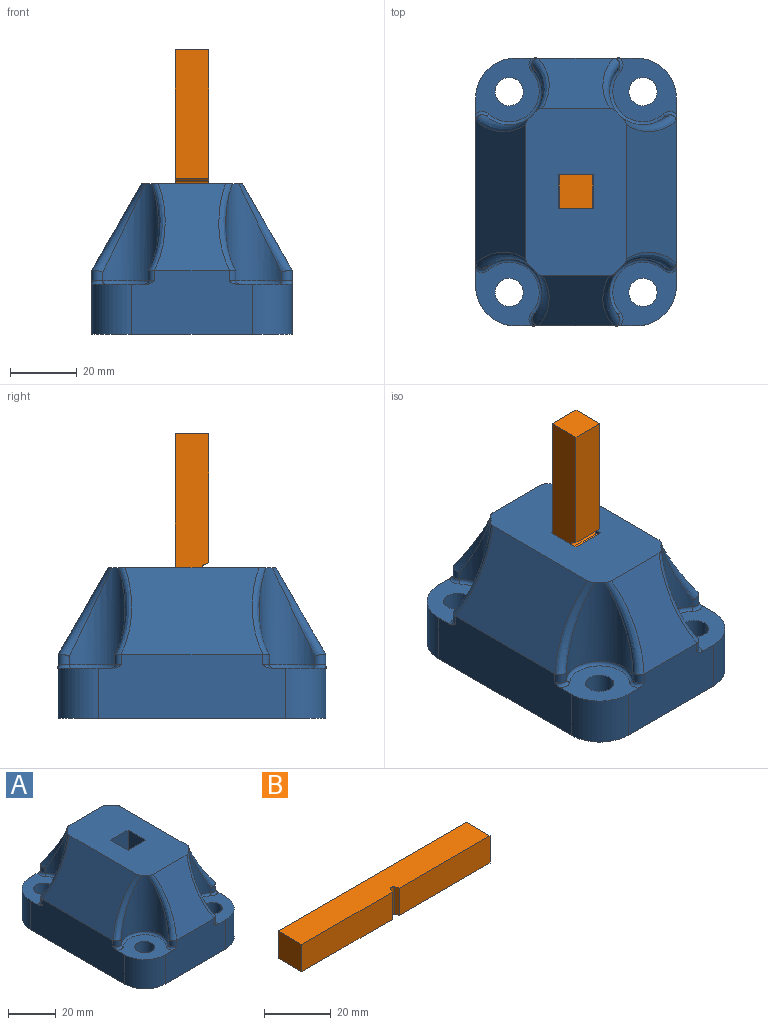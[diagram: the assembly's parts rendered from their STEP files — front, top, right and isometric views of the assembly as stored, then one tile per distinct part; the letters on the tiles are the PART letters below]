
ASSEMBLY  parts=2 mates=1
PART A: 59 faces, bbox 64.3x84.3x46.3 mm
  f0: plane 25.99x22.59mm, normal (0,0.87,0.5), area 532mm2, adj f8,f13,f31,f32,f35,f36
  f1: plane 42.59x25.99mm, normal (-0.87,0,0.5), area 1132mm2, adj f8,f11,f33,f34,f45,f46
  f2: cylinder r=12mm len=15mm, axis (0,0,-1), area 282.7mm2, adj f9,f11,f13,f29
  f3: plane 42.59x25.99mm, normal (0.87,0,0.5), area 1132mm2, adj f8,f10,f37,f38,f41,f42
  f4: cylinder r=12mm len=15mm, axis (0,0,1), area 282.7mm2, adj f9,f10,f13,f26
  f5: plane 25.99x22.59mm, normal (0,-0.87,0.5), area 532mm2, adj f8,f12,f39,f40,f43,f44
  f6: cylinder r=12mm len=15mm, axis (0,0,-1), area 282.7mm2, adj f9,f10,f12,f23
  f7: cylinder r=12mm len=15mm, axis (0,0,1), area 282.7mm2, adj f9,f11,f12,f20
  f8: plane 50.19x30.19mm, normal (0,0,1), area 1362.3mm2, adj f0,f1,f3,f5,f14,f15,f16,f17
  f9: plane 80x60mm, normal (0,0,-1), area 4454.7mm2, adj f2,f4,f6,f7,f10,f11,f12,f13
  f10: plane 56.31x19.33mm, normal (1,0,0), area 1010.9mm2, adj f3,f4,f6,f9,f23,f26,f37,f41
  f11: plane 56.31x19.33mm, normal (-1,0,0), area 1010.9mm2, adj f1,f2,f7,f9,f20,f29,f33,f45
  f12: plane 36.31x19.33mm, normal (0,-1,0), area 630.5mm2, adj f5,f6,f7,f9,f20,f23,f39,f43
  f13: plane 36.31x19.33mm, normal (0,1,0), area 630.5mm2, adj f0,f2,f4,f9,f26,f29,f31,f35
  f14: plane 40x10.2mm, normal (0,1,0), area 408mm2, adj f8,f15,f17,f18
  f15: plane 40x10.2mm, normal (-1,0,0), area 408mm2, adj f8,f14,f16,f18
  f16: plane 40x10.2mm, normal (0,-1,0), area 408mm2, adj f8,f15,f17,f18
  f17: plane 40x10.2mm, normal (1,0,0), area 408mm2, adj f8,f14,f16,f18
  f18: plane 10.2x10.2mm, normal (0,0,1), area 104mm2, adj f14,f15,f16,f17
  f19: cylinder r=4.2mm len=15mm, axis (0,0,1), area 395.8mm2, adj f9,f20
  f20: plane 19x19mm, normal (0,0,1), area 226.1mm2, adj f7,f11,f12,f19,f47,f48,f49
  f21: cylinder r=10mm len=29mm, axis (0,0,1), area 511.6mm2, adj f8,f43,f44,f45,f46,f48
  f22: cylinder r=4.2mm len=15mm, axis (0,0,1), area 395.8mm2, adj f9,f23
  f23: plane 19x19mm, normal (0,0,1), area 226.1mm2, adj f6,f10,f12,f22,f50,f51,f52
  f24: cylinder r=10mm len=29mm, axis (0,0,1), area 511.6mm2, adj f8,f39,f40,f41,f42,f51
  f25: cylinder r=4.2mm len=15mm, axis (0,0,1), area 395.8mm2, adj f9,f26
  f26: plane 19x19mm, normal (0,0,1), area 226.1mm2, adj f4,f10,f13,f25,f53,f54,f55
  f27: cylinder r=10mm len=29mm, axis (0,0,1), area 511.6mm2, adj f8,f35,f36,f37,f38,f54
  f28: cylinder r=4.2mm len=15mm, axis (0,0,1), area 395.8mm2, adj f9,f29
  f29: plane 19x19mm, normal (0,0,1), area 226.1mm2, adj f2,f11,f13,f28,f56,f57,f58
  f30: cylinder r=10mm len=29mm, axis (0,0,1), area 511.6mm2, adj f8,f31,f32,f33,f34,f57
  f31: cylinder r=2mm len=3.33mm, axis (0,0,1), area 13.7mm2, adj f0,f13,f30,f32,f56
  f32: bspline ~28.08x16.15mm, area 97.8mm2, adj f0,f8,f30,f31
  f33: cylinder r=2mm len=3.33mm, axis (0,0,1), area 13.7mm2, adj f1,f11,f30,f34,f58
  f34: bspline ~28.08x16.15mm, area 97.8mm2, adj f1,f8,f30,f33
  f35: cylinder r=2mm len=3.33mm, axis (0,0,1), area 13.7mm2, adj f0,f13,f27,f36,f55
  f36: bspline ~28.08x16.15mm, area 97.8mm2, adj f0,f8,f27,f35
  f37: cylinder r=2mm len=3.33mm, axis (0,0,1), area 13.7mm2, adj f3,f10,f27,f38,f53
  f38: bspline ~28.08x16.15mm, area 97.8mm2, adj f3,f8,f27,f37
  f39: cylinder r=2mm len=3.33mm, axis (0,0,1), area 13.7mm2, adj f5,f12,f24,f40,f50
  f40: bspline ~28.08x16.15mm, area 97.8mm2, adj f5,f8,f24,f39
  f41: cylinder r=2mm len=3.33mm, axis (0,0,1), area 13.7mm2, adj f3,f10,f24,f42,f52
  f42: bspline ~28.08x16.15mm, area 97.8mm2, adj f3,f8,f24,f41
  f43: cylinder r=2mm len=3.33mm, axis (0,0,1), area 13.7mm2, adj f5,f12,f21,f44,f49
  f44: bspline ~28.08x16.15mm, area 97.8mm2, adj f5,f8,f21,f43
  f45: cylinder r=2mm len=3.33mm, axis (0,0,1), area 13.7mm2, adj f1,f11,f21,f46,f47
  f46: bspline ~28.08x16.15mm, area 97.8mm2, adj f1,f8,f21,f45
  f47: torus R=3mm, axis (0,0,1), area 6.9mm2, adj f11,f20,f45,f48
  f48: torus R=9mm, axis (0,0,1), area 45.9mm2, adj f20,f21,f47,f49
  f49: torus R=3mm, axis (0,0,1), area 6.9mm2, adj f12,f20,f43,f48
  f50: torus R=3mm, axis (0,0,1), area 6.9mm2, adj f12,f23,f39,f51
  f51: torus R=9mm, axis (0,0,1), area 45.9mm2, adj f23,f24,f50,f52
  f52: torus R=3mm, axis (0,0,1), area 6.9mm2, adj f10,f23,f41,f51
  f53: torus R=3mm, axis (0,0,1), area 6.9mm2, adj f10,f26,f37,f54
  f54: torus R=9mm, axis (0,0,1), area 45.9mm2, adj f26,f27,f53,f55
  f55: torus R=3mm, axis (0,0,1), area 6.9mm2, adj f13,f26,f35,f54
  f56: torus R=3mm, axis (0,0,1), area 6.9mm2, adj f13,f29,f31,f57
  f57: torus R=9mm, axis (0,0,1), area 45.9mm2, adj f29,f30,f56,f58
  f58: torus R=3mm, axis (0,0,1), area 6.9mm2, adj f11,f29,f33,f57
PART B: 10 faces, bbox 80x10x10 mm
  f0: plane 10x1.38mm, normal (-0.92,-0.38,0), area 15mm2, adj f1,f7,f8,f9
  f1: plane 38.5x10mm, normal (0,-1,0), area 385mm2, adj f0,f2,f8,f9
  f2: plane 10x10mm, normal (1,0,0), area 100mm2, adj f1,f3,f8,f9
  f3: plane 80x10mm, normal (0,1,0), area 800mm2, adj f2,f4,f8,f9
  f4: plane 10x10mm, normal (-1,0,0), area 100mm2, adj f3,f5,f8,f9
  f5: plane 38.5x10mm, normal (0,-1,0), area 385mm2, adj f4,f6,f8,f9
  f6: plane 10x1.38mm, normal (0.92,-0.38,0), area 15mm2, adj f5,f7,f8,f9
  f7: cylinder r=1mm len=10mm, axis (0,0,-1), area 23.6mm2, adj f0,f6,f8,f9
  f8: plane 80x10mm, normal (0,0,1), area 795.8mm2, adj f0,f1,f2,f3,f4,f5,f6,f7
  f9: plane 80x10mm, normal (0,0,-1), area 795.8mm2, adj f0,f1,f2,f3,f4,f5,f6,f7
PLACE A at identity fixed
PLACE B rot(axis=(0,-1,0),90deg) t=(5,0,45)mm
MATE fastened B.f4 <-> A.f18  axis (0,0,-1) through (0,0,5)mm
